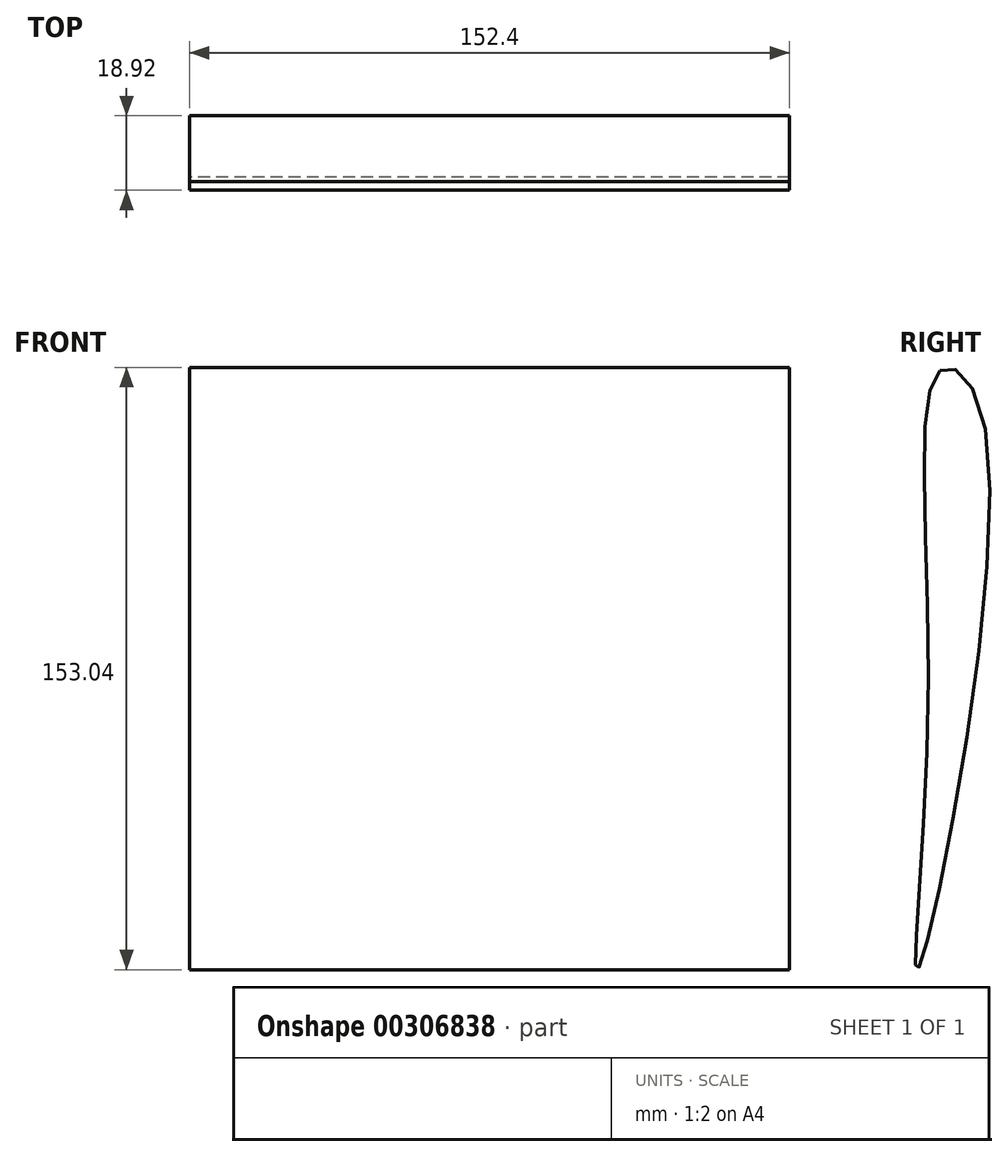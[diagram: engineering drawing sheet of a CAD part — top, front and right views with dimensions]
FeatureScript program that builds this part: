
annotation { "Feature Type Name" : "Feature", "Feature Type Description" : "" }
export const myFeature = defineFeature(function(context is Context, id is Id, definition is map)
    precondition{}
    {
        {
            var Q0;
            Q0=qCreatedBy(makeId("Right.planeOp"),FACE);
            var sketch = newSketch(context, id + "F0", { "sketchPlane" : qUnion([Q0])});
            skFitSpline(sketch, "E0", {"points": [v(3.27, 75.24) * mm, v(14.59, 61.8) * mm, v(-2.03, -76.46) * mm, v(0.33, -8.8) * mm, v(3.27, 75.24) * mm]});
            skSolve(sketch);
        }
        {
            var Q0;
            Q0=makeQuery(id+"F0.imprint","IMPRINT",FACE,{"disambiguationData":[TD([[makeQuery(id+"F0.imprint","IMPRINT",EDGE,{"derivedFrom":sQuery(id+"F0.wireOp",EDGE,"E0")}),-1.0]])]});
            extrude(context, id + "F1", {"entities" : qUnion([Q0]), "depth" : 76.2 * mm, "hasSecondDirection" : true, "secondDirectionOppositeDirection" : true, "secondDirectionDepth" : 76.2 * mm});
        }
    });
